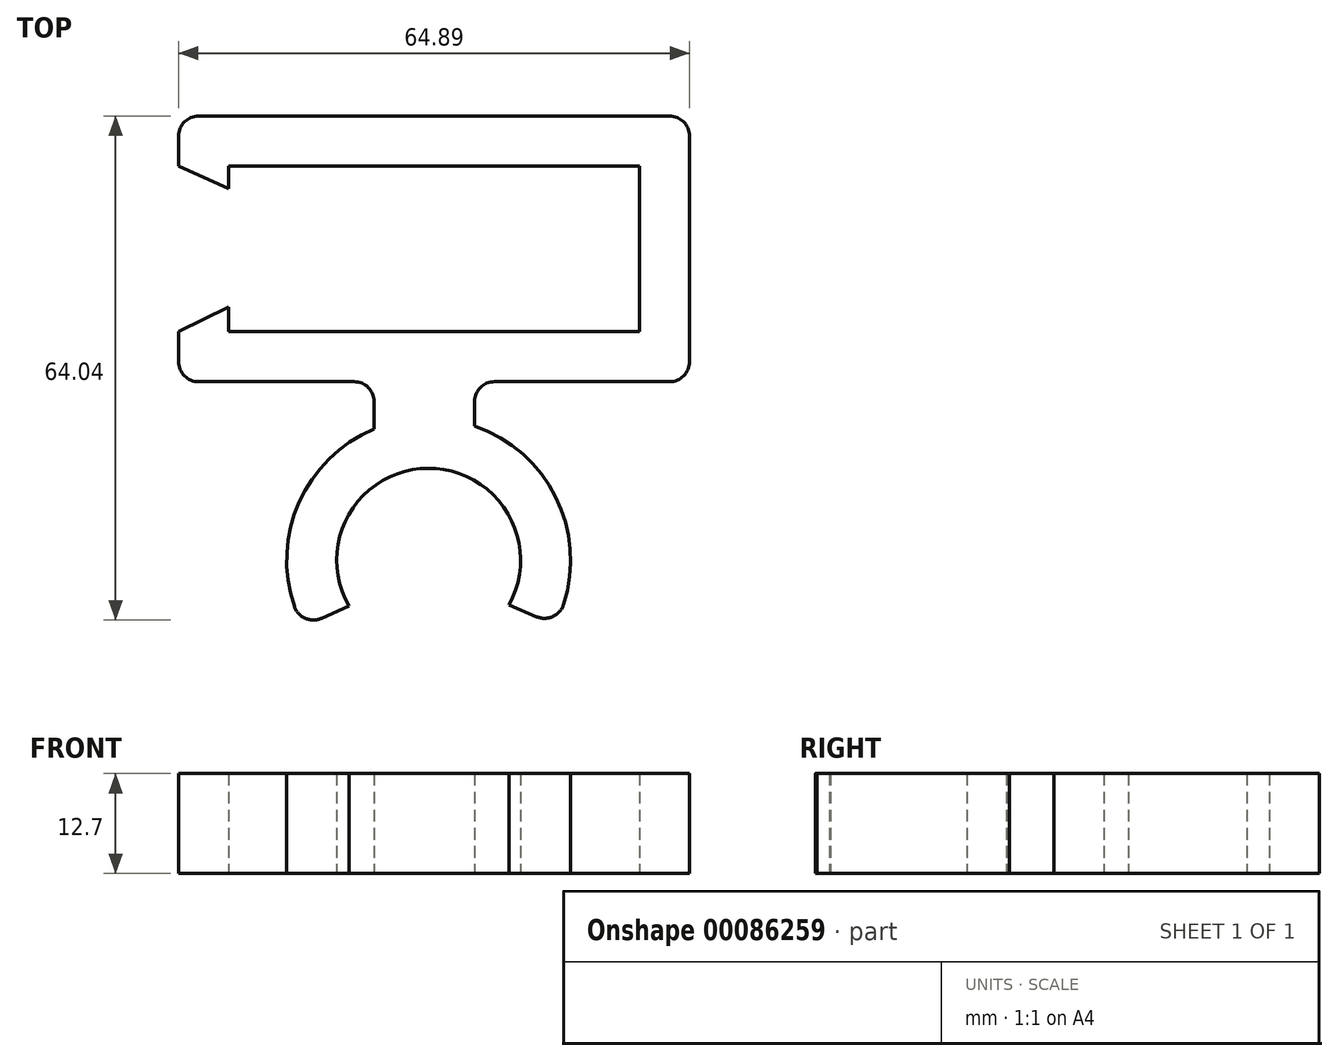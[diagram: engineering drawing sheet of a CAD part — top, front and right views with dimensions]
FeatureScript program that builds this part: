
annotation { "Feature Type Name" : "Feature", "Feature Type Description" : "" }
export const myFeature = defineFeature(function(context is Context, id is Id, definition is map)
    precondition{}
    {
        {
            var Q0;
            Q0=qCreatedBy(makeId("Top.planeOp"),FACE);
            var sketch = newSketch(context, id + "F0", { "sketchPlane" : qUnion([Q0])});
            skLineSegment(sketch, "E0.bottom", {"start": v(-57.17, 46.65) * mm, "end": v(-4.98, 46.65) * mm});
            skLineSegment(sketch, "E0.top", {"start": v(-57.17, 67.7) * mm, "end": v(-4.98, 67.7) * mm});
            skLineSegment(sketch, "E0.left", {"start": v(-57.17, 46.65) * mm, "end": v(-57.17, 49.77) * mm});
            skLineSegment(sketch, "E0.right", {"start": v(-4.98, 46.65) * mm, "end": v(-4.98, 67.7) * mm});
            skLineSegment(sketch, "E1.bottom", {"start": v(-63.52, 74.06) * mm, "end": v(1.37, 74.06) * mm});
            skLineSegment(sketch, "E1.top", {"start": v(-63.52, 40.3) * mm, "end": v(-38.69, 40.3) * mm});
            skLineSegment(sketch, "E1.left", {"start": v(-63.52, 74.06) * mm, "end": v(-63.52, 67.68) * mm});
            skLineSegment(sketch, "E1.right", {"start": v(1.37, 74.06) * mm, "end": v(1.37, 40.3) * mm});
            skArc(sketch, "E2", {"start": v(-38.69, 34.27) * mm, "mid": v(-48.73, 23.72) * mm, "end": v(-47.7, 9.2) * mm});
            skArc(sketch, "E3", {"start": v(-21.55, 11.94) * mm, "mid": v(-31.84, 29.3) * mm, "end": v(-41.9, 11.8) * mm});
            skLineSegment(sketch, "E4", {"start": v(-38.69, 34.27) * mm, "end": v(-38.69, 40.3) * mm});
            skLineSegment(sketch, "E5", {"start": v(-25.93, 34.68) * mm, "end": v(-25.93, 40.3) * mm});
            skLineSegment(sketch, "E6.trimOffspring", {"start": v(-25.93, 40.3) * mm, "end": v(1.37, 40.3) * mm});
            skLineSegment(sketch, "E7", {"start": v(-63.52, 46.65) * mm, "end": v(-57.17, 49.77) * mm});
            skLineSegment(sketch, "E8", {"start": v(-63.52, 67.68) * mm, "end": v(-57.17, 64.85) * mm});
            skLineSegment(sketch, "E9.trimOffspring", {"start": v(-57.17, 64.85) * mm, "end": v(-57.17, 67.7) * mm});
            skLineSegment(sketch, "E10.trimOffspring", {"start": v(-63.52, 46.65) * mm, "end": v(-63.52, 40.3) * mm});
            skLineSegment(sketch, "E11", {"start": v(-47.7, 9.2) * mm, "end": v(-41.9, 11.8) * mm});
            skLineSegment(sketch, "E12", {"start": v(-21.55, 11.94) * mm, "end": v(-15.68, 9.44) * mm});
            skArc(sketch, "E13.trimOffspring", {"start": v(-15.68, 9.44) * mm, "mid": v(-15.05, 24.4) * mm, "end": v(-25.93, 34.68) * mm});
            skSolve(sketch);
        }
        {
            var Q0;
            Q0=makeQuery(id+"F0.imprint","IMPRINT",FACE,{"disambiguationData":[TD([[makeQuery(id+"F0.imprint","IMPRINT",EDGE,{"derivedFrom":sQuery(id+"F0.wireOp",EDGE,"E0.bottom")}),-1.0]])]});
            extrude(context, id + "F1", {"entities" : qUnion([Q0]), "depth" : 12.7 * mm});
        }
        {
            var Q0;
            Q0=makeQuery(id+"F1.opExtrude","SWEPT_EDGE",EDGE,{"disambiguationData":[OSD([sQuery(id+"F0.wireOp",EDGE,"E1.bottom"),sQuery(id+"F0.wireOp",EDGE,"E1.left")])]});
            var Q1;
            Q1=makeQuery(id+"F1.opExtrude","SWEPT_EDGE",EDGE,{"disambiguationData":[OSD([sQuery(id+"F0.wireOp",EDGE,"E1.top"),sQuery(id+"F0.wireOp",EDGE,"E10.trimOffspring")])]});
            var Q2;
            Q2=makeQuery(id+"F1.opExtrude","SWEPT_EDGE",EDGE,{"disambiguationData":[OSD([sQuery(id+"F0.wireOp",EDGE,"E1.top"),sQuery(id+"F0.wireOp",EDGE,"E4")])]});
            var Q3;
            Q3=makeQuery(id+"F1.opExtrude","SWEPT_EDGE",EDGE,{"disambiguationData":[OSD([sQuery(id+"F0.wireOp",EDGE,"E5"),sQuery(id+"F0.wireOp",EDGE,"E6.trimOffspring")])]});
            var Q4;
            Q4=makeQuery(id+"F1.opExtrude","SWEPT_EDGE",EDGE,{"disambiguationData":[OSD([sQuery(id+"F0.wireOp",EDGE,"E1.right"),sQuery(id+"F0.wireOp",EDGE,"E6.trimOffspring")])]});
            var Q5;
            Q5=makeQuery(id+"F1.opExtrude","SWEPT_EDGE",EDGE,{"disambiguationData":[OSD([sQuery(id+"F0.wireOp",EDGE,"E1.bottom"),sQuery(id+"F0.wireOp",EDGE,"E1.right")])]});
            fillet(context, id + "F2", {"entities" : qUnion([Q0, Q1, Q2, Q3, Q4, Q5]), "radius" : 2.54 * mm, "tangentPropagation" : true, "allowEdgeOverflow" : false});
        }
        {
            var Q0;
            Q0=makeQuery(id+"F1.opExtrude","SWEPT_EDGE",EDGE,{"disambiguationData":[OSD([sQuery(id+"F0.wireOp",EDGE,"E12"),sQuery(id+"F0.wireOp",EDGE,"E13.trimOffspring")])]});
            var Q1;
            Q1=makeQuery(id+"F1.opExtrude","SWEPT_EDGE",EDGE,{"disambiguationData":[OSD([sQuery(id+"F0.wireOp",EDGE,"E2"),sQuery(id+"F0.wireOp",EDGE,"E11")])]});
            fillet(context, id + "F3", {"entities" : qUnion([Q0, Q1]), "radius" : 2.54 * mm, "tangentPropagation" : true, "allowEdgeOverflow" : false});
        }
    });
